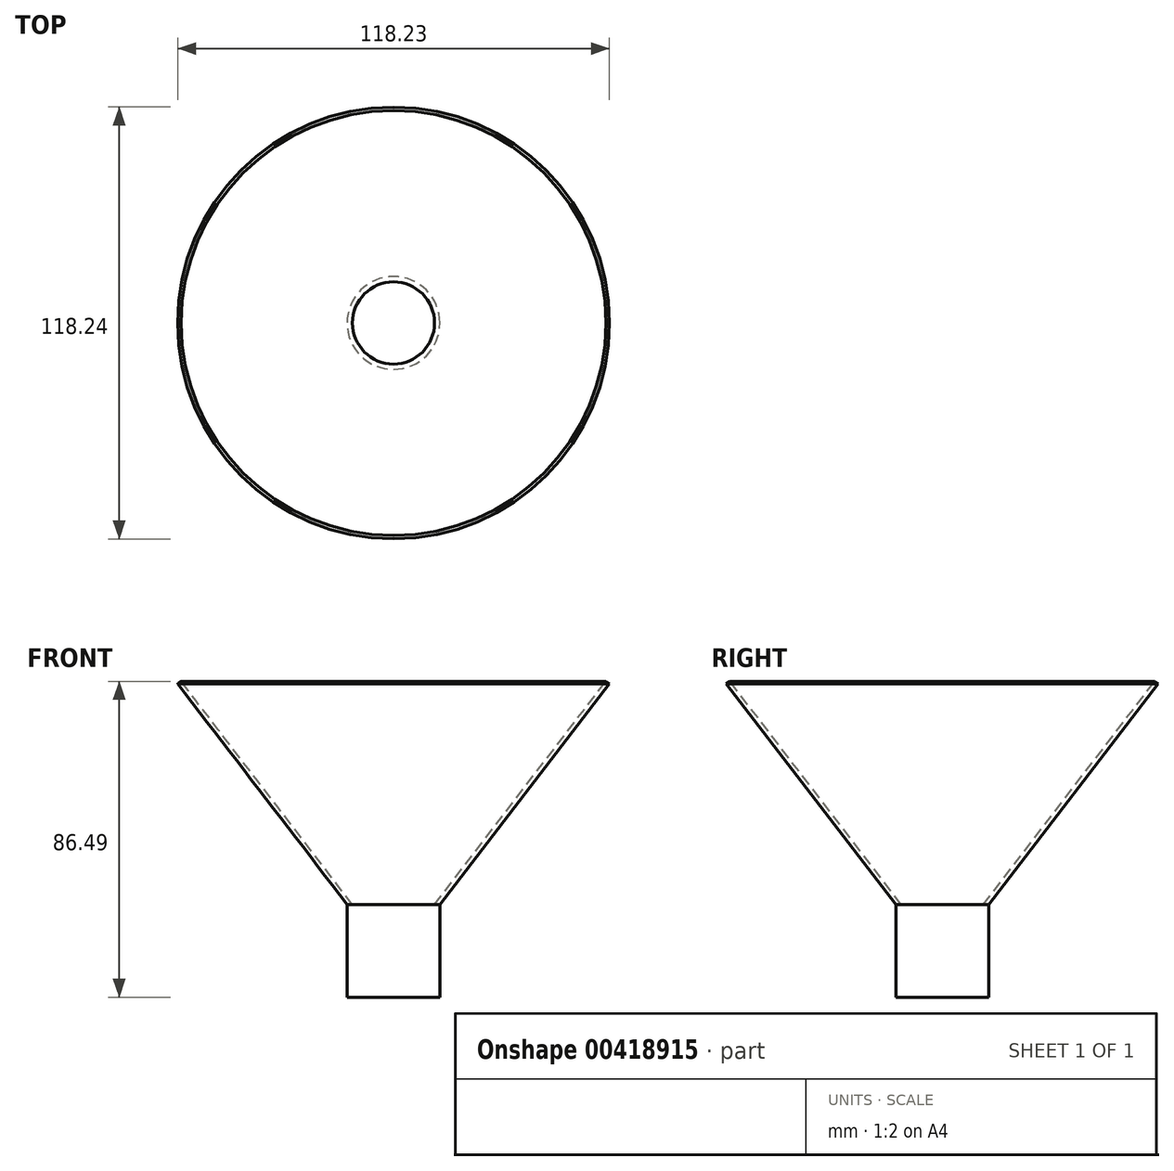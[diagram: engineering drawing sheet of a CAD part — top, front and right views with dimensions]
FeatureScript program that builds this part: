
annotation { "Feature Type Name" : "Feature", "Feature Type Description" : "" }
export const myFeature = defineFeature(function(context is Context, id is Id, definition is map)
    precondition{}
    {
        {
            var Q0;
            Q0=qCreatedBy(makeId("Front.planeOp"),FACE);
            var sketch = newSketch(context, id + "F0", { "sketchPlane" : qUnion([Q0])});
            skLineSegment(sketch, "E0", {"start": v(18.28, -26.72) * mm, "end": v(18.28, -1.32) * mm});
            skLineSegment(sketch, "E1", {"start": v(18.28, -1.32) * mm, "end": v(64.7, 59.11) * mm});
            skLineSegment(sketch, "E2", {"start": v(18.28, -26.72) * mm, "end": v(5.58, -26.72) * mm});
            skLineSegment(sketch, "E3", {"start": v(5.58, -26.72) * mm, "end": v(5.58, -1.32) * mm});
            skLineSegment(sketch, "E4", {"start": v(5.58, -1.32) * mm, "end": v(16.82, -1.32) * mm});
            skLineSegment(sketch, "E5", {"start": v(16.82, -1.32) * mm, "end": v(63.74, 59.77) * mm});
            skLineSegment(sketch, "E6", {"start": v(63.74, 59.77) * mm, "end": v(64.7, 59.11) * mm});
            skSolve(sketch);
        }
        {
            var Q0;
            Q0=makeQuery(id+"F0.imprint","IMPRINT",FACE,{"disambiguationData":[TD([[makeQuery(id+"F0.imprint","IMPRINT",EDGE,{"derivedFrom":sQuery(id+"F0.wireOp",EDGE,"E0")}),1.0]])]});
            var Q1;
            Q1=sQuery(id+"F0.wireOp",EDGE,"E3");
            revolve(context, id + "F1", {"entities" : qUnion([Q0]), "axis" : qUnion([Q1]), "revolveType" : RevolveType.FULL});
        }
    });
